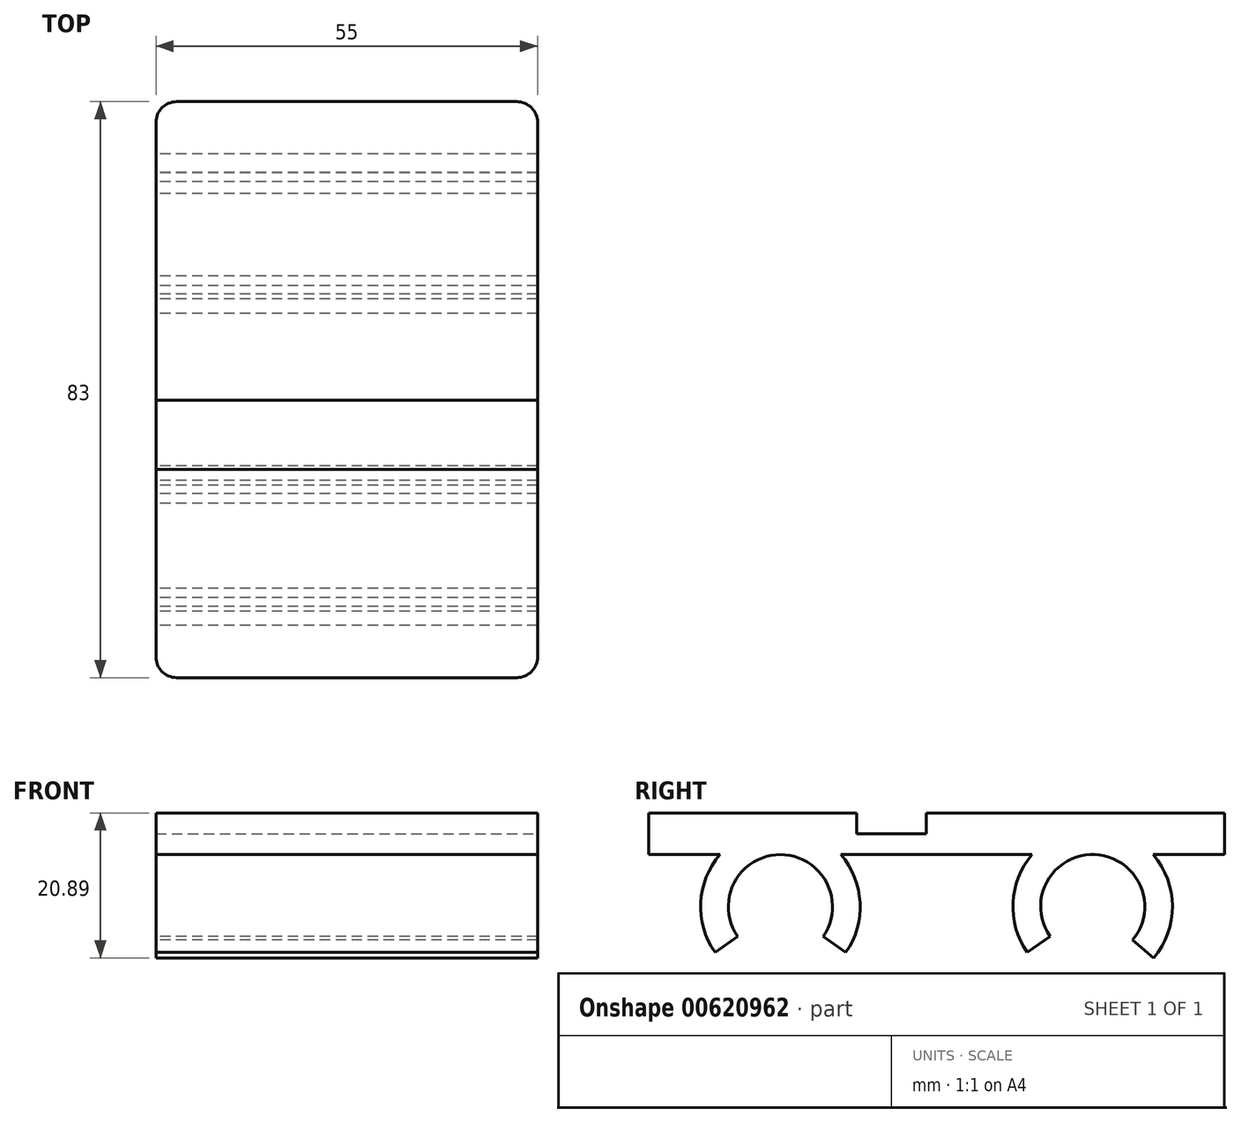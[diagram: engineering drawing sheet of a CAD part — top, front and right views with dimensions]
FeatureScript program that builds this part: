
annotation { "Feature Type Name" : "Feature", "Feature Type Description" : "" }
export const myFeature = defineFeature(function(context is Context, id is Id, definition is map)
    precondition{}
    {
        {
            var Q0;
            Q0=qCreatedBy(makeId("Top.planeOp"),FACE);
            var sketch = newSketch(context, id + "F0", { "sketchPlane" : qUnion([Q0])});
            skLineSegment(sketch, "E0.bottom", {"start": v(3, 0) * mm, "end": v(52, 0) * mm});
            skLineSegment(sketch, "E0.top", {"start": v(3, 83) * mm, "end": v(52, 83) * mm});
            skLineSegment(sketch, "E0.left", {"start": v(0, 3) * mm, "end": v(0, 80) * mm});
            skLineSegment(sketch, "E0.right", {"start": v(55, 3) * mm, "end": v(55, 80) * mm});
            skPoint(sketch, "E1.visualSharp", {"position": v(0, 83) * mm});
            skArc(sketch, "E1.filletArc", {"start": v(3, 83) * mm, "mid": v(0.88, 82.12) * mm, "end": v(0, 80) * mm});
            skPoint(sketch, "E2.visualSharp", {"position": v(55, 83) * mm});
            skArc(sketch, "E2.filletArc", {"start": v(55, 80) * mm, "mid": v(54.12, 82.12) * mm, "end": v(52, 83) * mm});
            skPoint(sketch, "E3.visualSharp", {"position": v(55, 0) * mm});
            skArc(sketch, "E3.filletArc", {"start": v(52, 0) * mm, "mid": v(54.12, 0.88) * mm, "end": v(55, 3) * mm});
            skPoint(sketch, "E4.visualSharp", {"position": v(0, 0) * mm});
            skArc(sketch, "E4.filletArc", {"start": v(0, 3) * mm, "mid": v(0.88, 0.88) * mm, "end": v(3, 0) * mm});
            skSolve(sketch);
        }
        {
            var Q0;
            Q0 = qSketchRegion(id + "F0", true);
            extrude(context, id + "F1", {"entities" : qUnion([Q0]), "depth" : 6 * mm, "offsetDistance" : 25 * mm});
        }
        {
            var Q0;
            Q0=makeQuery(id+"F1.opExtrude","CAP_FACE",FACE,{"disambiguationData":[OSD([sQuery(id+"F0.wireOp",EDGE,"E0.bottom"),sQuery(id+"F0.wireOp",EDGE,"E0.top"),sQuery(id+"F0.wireOp",EDGE,"E0.left"),sQuery(id+"F0.wireOp",EDGE,"E0.right"),sQuery(id+"F0.wireOp",EDGE,"E1.filletArc"),sQuery(id+"F0.wireOp",EDGE,"E2.filletArc"),sQuery(id+"F0.wireOp",EDGE,"E3.filletArc"),sQuery(id+"F0.wireOp",EDGE,"E4.filletArc")])],"isStart":false});
            var sketch = newSketch(context, id + "F2", { "sketchPlane" : qUnion([Q0])});
            skLineSegment(sketch, "E5", {"start": v(0, 30) * mm, "end": v(55, 30) * mm});
            skLineSegment(sketch, "E6", {"start": v(55, 30) * mm, "end": v(55, 40) * mm});
            skLineSegment(sketch, "E7", {"start": v(55, 40) * mm, "end": v(0, 40) * mm});
            skLineSegment(sketch, "E8", {"start": v(0, 40) * mm, "end": v(0, 30) * mm});
            skSolve(sketch);
        }
        {
            var Q0;
            Q0 = qSketchRegion(id + "F2", true);
            extrude(context, id + "F3", {"entities" : qUnion([Q0]), "operationType" : NewBodyOperationType.REMOVE, "oppositeDirection" : true, "depth" : 3 * mm, "offsetDistance" : 25 * mm});
        }
        {
            var Q0;
            Q0=makeQuery(id+"F1.opExtrude","SWEPT_FACE",FACE,{"disambiguationData":[OSD([sQuery(id+"F0.wireOp",EDGE,"E0.left")])]});
            var sketch = newSketch(context, id + "F4", { "sketchPlane" : qUnion([Q0])});
            skLineSegment(sketch, "E9", {"start": v(-101.08, -7.5) * mm, "end": v(11.48, -7.5) * mm, "construction": true});
            skArc(sketch, "E10", {"start": v(-57.86, -11.8) * mm, "mid": v(-64.33, 0) * mm, "end": v(-69.75, -12.32) * mm});
            skArc(sketch, "E11", {"start": v(-12.86, -11.8) * mm, "mid": v(-19, 0) * mm, "end": v(-25.14, -11.8) * mm});
            skArc(sketch, "E12", {"start": v(-54.58, -14.1) * mm, "mid": v(-64.5, 3.99) * mm, "end": v(-72.8, -14.9) * mm});
            skArc(sketch, "E13", {"start": v(-9.58, -14.1) * mm, "mid": v(-19, 4) * mm, "end": v(-28.42, -14.1) * mm});
            skLineSegment(sketch, "E14", {"start": v(-64, -7.5) * mm, "end": v(-75.7, -17.32) * mm, "construction": true});
            skLineSegment(sketch, "E15", {"start": v(-64, -7.5) * mm, "end": v(-51.29, -16.4) * mm, "construction": true});
            skLineSegment(sketch, "E16", {"start": v(-19, -7.5) * mm, "end": v(-31, -15.9) * mm, "construction": true});
            skLineSegment(sketch, "E17", {"start": v(-19, -7.5) * mm, "end": v(-6.73, -16.1) * mm, "construction": true});
            skLineSegment(sketch, "E18", {"start": v(-69.75, -12.32) * mm, "end": v(-72.8, -14.9) * mm});
            skLineSegment(sketch, "E19", {"start": v(-57.86, -11.8) * mm, "end": v(-54.58, -14.1) * mm});
            skLineSegment(sketch, "E20", {"start": v(-25.14, -11.8) * mm, "end": v(-28.42, -14.1) * mm});
            skLineSegment(sketch, "E21", {"start": v(-12.86, -11.8) * mm, "end": v(-9.58, -14.1) * mm});
            skLineSegment(sketch, "E22.0", {"start": v(0, 6) * mm, "end": v(0, 0) * mm, "construction": true});
            skLineSegment(sketch, "E22.1", {"start": v(-83, 6) * mm, "end": v(-83, 0) * mm, "construction": true});
            skLineSegment(sketch, "E23", {"start": v(0, 0) * mm, "end": v(0, -7.5) * mm, "construction": true});
            skLineSegment(sketch, "E24", {"start": v(-83, 0) * mm, "end": v(-83, -7.5) * mm, "construction": true});
            skLineSegment(sketch, "E25", {"start": v(0, -7.5) * mm, "end": v(-19, -7.5) * mm, "construction": true});
            skLineSegment(sketch, "E26", {"start": v(-83, -7.5) * mm, "end": v(-64, -7.5) * mm, "construction": true});
            skSolve(sketch);
        }
        {
            var Q0;
            Q0 = qSketchRegion(id + "F4", true);
            var Q1;
            Q1=makeQuery(id+"F1.opExtrude","SWEPT_FACE",FACE,{"disambiguationData":[OSD([sQuery(id+"F0.wireOp",EDGE,"E0.right")])]});
            var Q2;
            Q2=makeQuery(id+"F1.opExtrude","SWEPT_BODY",BODY,{"disambiguationData":[OSD([sQuery(id+"F0.wireOp",EDGE,"E0.bottom"),sQuery(id+"F0.wireOp",EDGE,"E0.top"),sQuery(id+"F0.wireOp",EDGE,"E0.left"),sQuery(id+"F0.wireOp",EDGE,"E0.right"),sQuery(id+"F0.wireOp",EDGE,"E1.filletArc"),sQuery(id+"F0.wireOp",EDGE,"E2.filletArc"),sQuery(id+"F0.wireOp",EDGE,"E3.filletArc"),sQuery(id+"F0.wireOp",EDGE,"E4.filletArc")])]});
            extrude(context, id + "F5", {"entities" : qUnion([Q0]), "operationType" : NewBodyOperationType.ADD, "endBound" : BoundingType.UP_TO_SURFACE, "oppositeDirection" : true, "depth" : 50 * mm, "endBoundEntityFace" : qUnion([Q1]), "endBoundEntityBody" : qUnion([Q2]), "offsetDistance" : 25 * mm});
        }
    });
